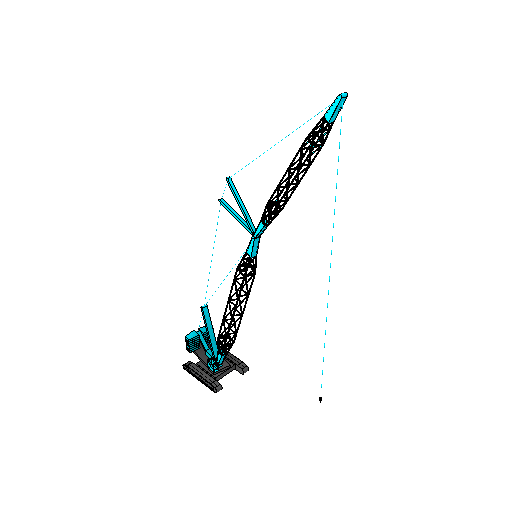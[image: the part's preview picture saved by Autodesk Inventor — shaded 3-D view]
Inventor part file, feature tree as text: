
AUTODESK INVENTOR PART (.ipt)
format: ipt  version: 2025.2 (Build 292293000, 293)  size: 1,781,248 bytes
history: native  units: mm
features: extrude x33, projected_geometry x15, plane x8, sketch x6, chamfer x4, sweep x4, other x3, pattern_linear x2, mirror x2, shell x2, revolve x1
ambient origin geometry x8: Origin, YZ Plane, XZ Plane, XY Plane, X Axis, Y Axis, Z Axis, Center Point
bodies: Solid7 (feature_tree), Solid9 (feature_tree), Solid10 (feature_tree), Solid11 (feature_tree), Solid12 (feature_tree), Solid13 (feature_tree), Solid14 (feature_tree), Solid15 (feature_tree)
feature tree (80):
  other  "FRAME"
  sketch  "Sketch1"  dims[d49=7895.0mm d50=650.0mm]
  extrude  "Extrusion1"  Depth=650.0mm
  extrude  "Extrusion2"  Depth=80.0mm
  extrude  "Extrusion3"  Depth=650.0mm
  extrude  "Extrusion4"  Depth=120.0mm
  pattern_linear  "Rectangular Pattern1"  Count1=27  [1 undecoded]
  revolve  "Revolution1"  [1 undecoded]
  extrude  "Extrusion5"  Depth=10.0mm
  extrude  "Extrusion6"  Depth=10.0mm
  extrude  "Extrusion7"  Depth=10.0mm
  plane  "Work Plane1"
  extrude  "Extrusion8"  Depth=10.0mm
  extrude  "Extrusion9"  Depth=10.0mm
  chamfer  "Chamfer1"  Distance=150.0mm
  chamfer  "Chamfer2"  Distance=3050.0mm
  extrude  "Extrusion10"  Depth=10.0mm TaperAngle=0.0deg
  extrude  "Extrusion11"  Depth=10.0mm TaperAngle=0.0deg
  pattern_linear  "Rectangular Pattern2"  Count1=750 Spacing1=0.0mm
  mirror  "Mirror1"
  plane  "Work Plane2"
  extrude  "Extrusion13"  Depth=10.0mm
  extrude  "Extrusion12"  Depth=10.0mm
  extrude  "Extrusion14"  Depth=10.0mm TaperAngle=0.0deg
  extrude  "Extrusion15"  Depth=10.0mm
  extrude  "Extrusion16"  TaperAngle=90.0deg  [1 undecoded]
  extrude  "Extrusion17"  Depth=10.0mm
  extrude  "Extrusion19"  Depth=10.0mm
  plane  "Work Plane3"
  extrude  "Extrusion20"  Depth=10.0mm
  extrude  "Extrusion21"  Depth=250.0mm
  extrude  "Extrusion22"  Depth=10.0mm
  shell  "Shell1"  Thickness=7500.0mm
  sketch  "Sketch17"  dims[d53=120.0mm d54=650.0mm]
  extrude  "Extrusion24"  TaperAngle=0.0deg  [1 undecoded]
  extrude  "Extrusion36"  Depth=10.0mm
  extrude  "Extrusion25"  Depth=10.0mm
  extrude  "Extrusion26"  Depth=10.0mm
  extrude  "Extrusion27"  Depth=10.0mm
  plane  "Work Plane4"
  extrude  "Extrusion28"  Depth=10.0mm
  extrude  "Extrusion29"  Depth=10.0mm
  shell  "Shell2"  Thickness=500.0mm
  extrude  "Extrusion30"  [1 undecoded]
  extrude  "Extrusion31"  Depth=10.0mm
  plane  "Work Plane5"
  extrude  "Extrusion33"  Depth=10.0mm
  extrude  "Extrusion34"  Depth=10.0mm
  sweep  "Sweep1"
  plane  "Work Plane6"
  sweep  "Sweep2"
  plane  "Work Plane7"
  sweep  "Sweep3"
  plane  "Work Plane8"
  sweep  "Sweep4"
  extrude  "Extrusion35"  Depth=10.0mm TaperAngle=0.0deg
  chamfer  "Chamfer3"  Distance=200.0mm Angle=45.0deg
  chamfer  "Chamfer4"  Distance=400.0mm Angle=45.0deg
  mirror  "Mirror2"
  sketch  "Sketch4"  dims[d51=80.0mm d52=80.0mm]
  projected_geometry  "Projected Loop1"
  projected_geometry  "Projected Loop3"
  projected_geometry  "Projected Loop4"
  projected_geometry  "Projected Loop5"
  projected_geometry  "Projected Loop6"
  projected_geometry  "Projected Loop7"
  projected_geometry  "Projected Loop8"
  other  "BOOM"
  other  "BACKMAST"
  projected_geometry  "Projected Loop10"
  projected_geometry  "Projected Loop11"
  projected_geometry  "Projected Loop12"
  sketch  "Sketch18"  dims[d55=80.0mm d56=120.0mm d58=270.0mm]
  projected_geometry  "Projected Loop13"
  sketch  "Sketch21"  dims[d59=270.0mm d60=650.0mm]
  projected_geometry  "Projected Loop16"
  projected_geometry  "Projected Loop17"
  projected_geometry  "Projected Loop18"
  sketch  "Sketch22"  dims[d62=750.0mm d63=120.0mm d64=950.0mm d66=120.0mm d71=2950.0mm d72=115.0mm d73=150.0mm d74=3050.0mm d77=7620.0mm d78=0.0mm d79=6500.0mm d80=0.0mm d81=7500.0mm d82=0.0mm d83=400.0mm d85=850.0mm d87=7500.0mm d88=0.0mm d89=120.0mm d91=560.0mm d92=90.0deg d93=440.0mm d94=1220.0mm d95=300.0mm d96=250.0mm d97=50.0mm d98=7500.0mm d99=0.0mm d100=0.0mm d101=0.0mm d102=2000.0mm d104=2000.0mm d105=3400.0mm d107=1400.0mm d110=1000.0mm d111=6000.0mm d112=500.0mm d113=0.0mm d114=-1700.0mm d115=800.0mm d116=200.0mm d117=2525.0mm d118=800.0mm d119=0.0mm d120=900.0mm d121=2100.0mm d122=20.0mm d123=1750.0mm d124=0.0mm d125=200.0mm d126=450.0mm d127=45.0deg d128=400.0mm d129=1050.0mm d130=45.0deg d131=1600.0mm d132=2600.0mm d133=20.0mm d134=0.0mm d136=430.0mm d137=0.0mm d138=70.0mm d140=450.0mm d141=10.0mm d142=20.0mm d143=700.0mm d144=1040.0mm d145=1000.0mm d146=3280.0mm d147=200.0mm d148=6.108652mm d149=3750.0mm d150=200.0mm d151=-20.0mm d152=20.0mm d153=50.0mm d154=0.0mm d155=0.0mm d156=900.0mm d157=0.0mm d158=50.0mm d159=50.0mm d160=0.0mm d161=50.0mm d162=50.0mm d163=0.0mm d164=50.0mm d165=50.0mm d166=0.0mm d167=500.0mm d168=35000.0mm d169=7800.0mm d170=2000.0mm d171=2000.0mm d172=7800.0mm d173=1000.0mm d174=0.0mm d177=33000.0mm d180=2000.0mm d181=0.0mm d182=2000.0mm d183=0.0mm d184=10.0mm d185=0.0mm d186=500.0mm d187=6.981317mm d188=9700.0mm d190=50.0mm d191=1000.0mm d192=0.0mm d195=100.0mm d196=100.0mm d197=100.0mm d198=100.0mm d199=50.0mm d200=50.0mm d201=50.0mm d202=50.0mm d203=50.0mm d204=50.0mm d205=0.0mm d206=0.0mm d207=100.0mm d209=100.0mm d210=50.0mm d211=50.0mm d212=50.0mm d213=50.0mm d214=50.0mm d215=50.0mm d216=2605.134mm d217=0.0mm d218=30000.0mm d219=500.0mm d220=1500.0mm d221=7800.0mm d222=7800.0mm d224=800.0mm d225=0.0mm d226=1500.0mm d227=0.0mm d228=2000.0mm d229=0.0mm d230=10.0mm d231=0.0mm d232=100.0mm d233=100.0mm d234=100.0mm d235=100.0mm d236=50.0mm d237=50.0mm d238=50.0mm d239=50.0mm d240=50.0mm d241=50.0mm d242=0.0mm d243=0.0mm d244=100.0mm d245=100.0mm d246=100.0mm d247=50.0mm d248=50.0mm d249=50.0mm d250=50.0mm d251=50.0mm d252=50.0mm d253=0.0mm d254=0.0mm d257=13.962634mm d258=9000.0mm d259=9000.0mm d260=13.962634mm d266=50.0mm d267=0.0mm d268=0.0mm d269=50.0mm d270=0.0mm d271=0.0mm d272=500.0mm d273=500.0mm d274=0.0mm d275=500.0mm d276=500.0mm d277=0.0mm d279=700.0mm d281=50.0mm d282=0.0mm d283=0.0mm d284=200.0mm d285=400.0mm d286=150.0mm d287=0.0mm d288=80.0mm d289=0.0mm d290=0.0mm d291=15.0mm d292=2.0mm d293=8.726646mm d294=30.0mm d295=2.0mm d296=13.962634mm d297=50.0mm d298=50.0mm d299=50.0mm d300=50.0mm d301=100.0mm d302=100.0mm d303=100.0mm d304=100.0mm d305=50.0mm d306=50.0mm d307=50.0mm d308=50.0mm d309=100.0mm d310=0.0mm]
  projected_geometry  "Projected Loop19"
note: 5 required parameter values undecoded (feature->parameter linkage not recoverable at this tier; creation-order binding heuristic only, values carry confidence <= 0.55)